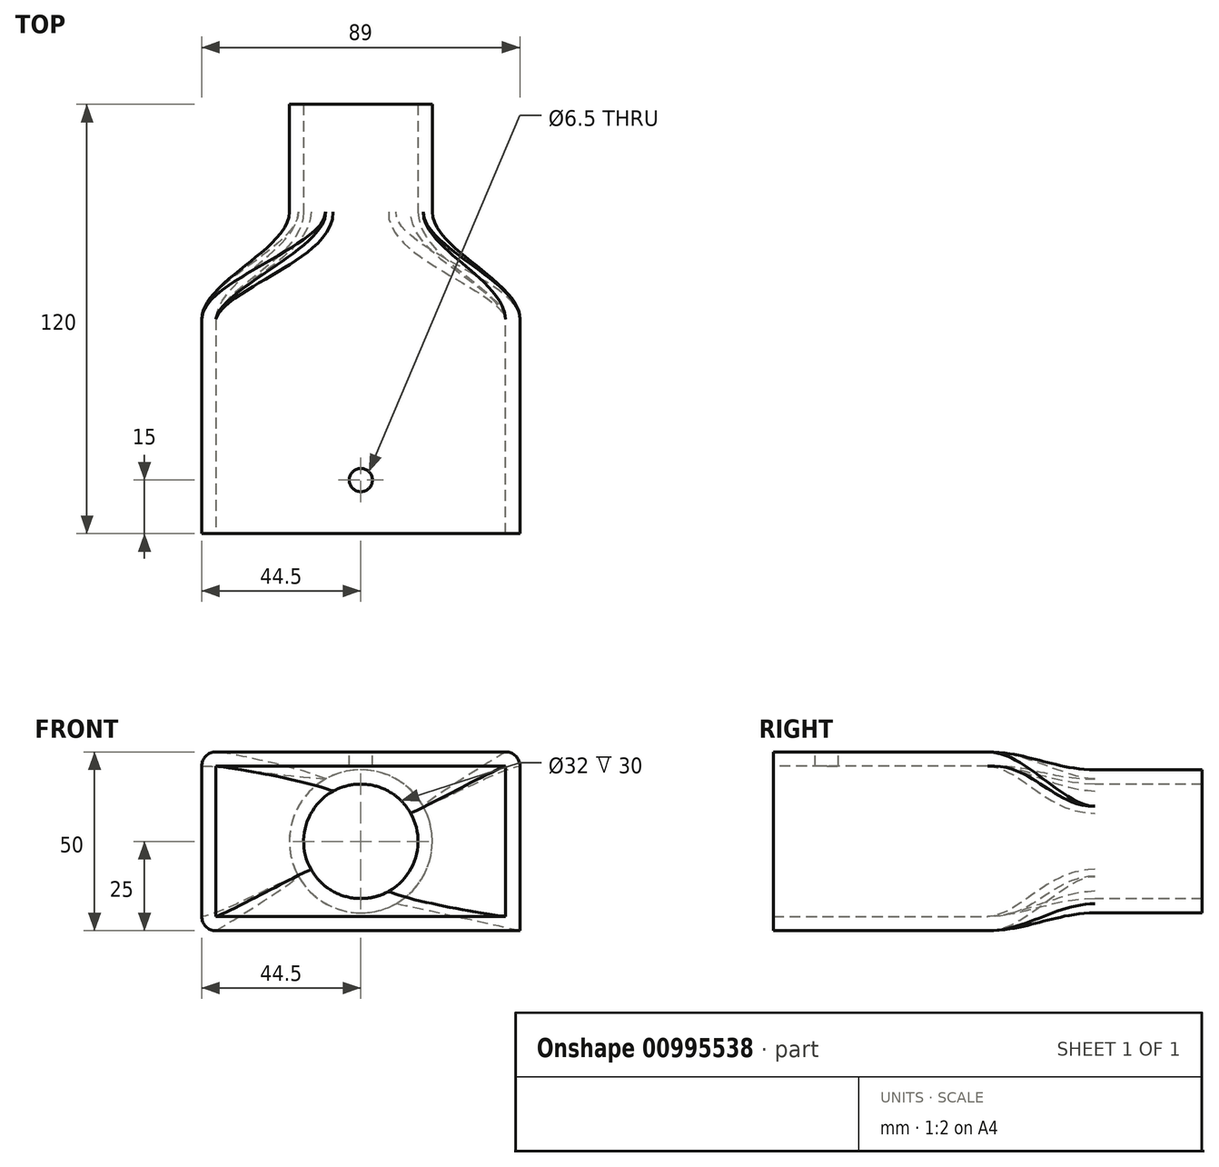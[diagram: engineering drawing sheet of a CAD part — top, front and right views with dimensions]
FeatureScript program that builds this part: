
annotation { "Feature Type Name" : "Feature", "Feature Type Description" : "" }
export const myFeature = defineFeature(function(context is Context, id is Id, definition is map)
    precondition{}
    {
        {
            var Q0;
            Q0=qCreatedBy(makeId("Front.planeOp"),FACE);
            var sketch = newSketch(context, id + "F0", { "sketchPlane" : qUnion([Q0])});
            skLineSegment(sketch, "E0.bottom", {"start": v(40.5, -21) * mm, "end": v(-40.5, -21) * mm, "construction": true});
            skLineSegment(sketch, "E0.top", {"start": v(40.5, 21) * mm, "end": v(-40.5, 21) * mm, "construction": true});
            skLineSegment(sketch, "E0.left", {"start": v(40.5, -21) * mm, "end": v(40.5, 21) * mm, "construction": true});
            skLineSegment(sketch, "E0.right", {"start": v(-40.5, -21) * mm, "end": v(-40.5, 21) * mm, "construction": true});
            skPoint(sketch, "E0.middle", {"position": v(0, 0) * mm});
            skLineSegment(sketch, "E1.0", {"start": v(44.5, 25) * mm, "end": v(-44.5, 25) * mm});
            skLineSegment(sketch, "E1.1", {"start": v(44.5, -25) * mm, "end": v(44.5, 25) * mm});
            skLineSegment(sketch, "E1.2", {"start": v(44.5, -25) * mm, "end": v(-44.5, -25) * mm});
            skLineSegment(sketch, "E1.3", {"start": v(-44.5, -25) * mm, "end": v(-44.5, 25) * mm});
            skSolve(sketch);
        }
        {
            var Q0;
            Q0 = qSketchRegion(id + "F0", true);
            extrude(context, id + "F1", {"entities" : qUnion([Q0]), "depth" : 60 * mm, "offsetDistance" : 25 * mm});
        }
        {
            var Q0;
            Q0=qCreatedBy(makeId("Front.planeOp"),FACE);
            cPlane(context, id + "F2", {"entities" : qUnion([Q0]), "cplaneType" : CPlaneType.OFFSET, "offset" : 30 * mm, "oppositeDirection" : true, "width" : 150 * mm, "height" : 150 * mm});
        }
        {
            var Q0;
            Q0=qCreatedBy(id+"F2.planeOp",FACE);
            var sketch = newSketch(context, id + "F3", { "sketchPlane" : qUnion([Q0])});
            skCircle(sketch, "E2", {"center": v(0, 0) * mm, "radius": 20 * mm});
            skSolve(sketch);
        }
        {
            var Q1;
            Q1=makeQuery(id+"F1.opExtrude","CAP_FACE",FACE,{"disambiguationData":[OSD([sQuery(id+"F0.wireOp",EDGE,"E1.0"),sQuery(id+"F0.wireOp",EDGE,"E1.1"),sQuery(id+"F0.wireOp",EDGE,"E1.2"),sQuery(id+"F0.wireOp",EDGE,"E1.3")])],"isStart":true});
            var Q2;
            Q2 = qSketchRegion(id + "F3", true);
            loft(context, id + "F4", {"operationType" : NewBodyOperationType.ADD, "startCondition" : LoftEndDerivativeType.NORMAL_TO_PROFILE, "startMagnitude" : 1, "endCondition" : LoftEndDerivativeType.NORMAL_TO_PROFILE, "endMagnitude" : 1, "sheetProfilesArray" : [{ "sheetProfileEntities" : qUnion([Q1]) }, { "sheetProfileEntities" : qUnion([Q2]) }]});
        }
        {
            var Q0;
            Q0 = qSketchRegion(id + "F3", true);
            extrude(context, id + "F5", {"entities" : qUnion([Q0]), "operationType" : NewBodyOperationType.ADD, "oppositeDirection" : true, "depth" : 30 * mm, "offsetDistance" : 25 * mm, "hasSecondDirection" : true, "secondDirectionOppositeDirection" : false, "secondDirectionDepth" : 10 * mm});
        }
        {
            var Q0;
            Q0=makeQuery(id+"F4.opLoft","SWEPT_EDGE",EDGE,{"disambiguationData":[OSD([sQuery(id+"F0.wireOp",EDGE,"E1.0"),sQuery(id+"F0.wireOp",EDGE,"E1.2"),sQuery(id+"F0.wireOp",EDGE,"E1.3"),sQuery(id+"F3.wireOp",EDGE,"E2")])]});
            var Q1;
            Q1=makeQuery(id+"F4.opLoft","SWEPT_EDGE",EDGE,{"disambiguationData":[OSD([sQuery(id+"F0.wireOp",EDGE,"E1.1"),sQuery(id+"F0.wireOp",EDGE,"E1.2"),sQuery(id+"F0.wireOp",EDGE,"E1.3"),sQuery(id+"F3.wireOp",EDGE,"E2")])]});
            var Q2;
            Q2=makeQuery(id+"F4.opLoft","SWEPT_EDGE",EDGE,{"disambiguationData":[OSD([sQuery(id+"F0.wireOp",EDGE,"E1.0"),sQuery(id+"F0.wireOp",EDGE,"E1.1"),sQuery(id+"F0.wireOp",EDGE,"E1.2"),sQuery(id+"F3.wireOp",EDGE,"E2")])]});
            var Q3;
            Q3=makeQuery(id+"F4.opLoft","SWEPT_EDGE",EDGE,{"disambiguationData":[OSD([sQuery(id+"F0.wireOp",EDGE,"E1.0"),sQuery(id+"F0.wireOp",EDGE,"E1.1")])]});
            fillet(context, id + "F6", {"entities" : qUnion([Q0, Q1, Q2, Q3]), "radius" : 4 * mm, "tangentPropagation" : true, "allowEdgeOverflow" : false});
        }
        {
            var Q0;
            Q0=makeQuery(id+"F5.opExtrude","CAP_FACE",FACE,{"disambiguationData":[OSD([sQuery(id+"F3.wireOp",EDGE,"E2")])],"isStart":false});
            var Q1;
            Q1=makeQuery(id+"F1.opExtrude","CAP_FACE",FACE,{"disambiguationData":[OSD([sQuery(id+"F0.wireOp",EDGE,"E1.0"),sQuery(id+"F0.wireOp",EDGE,"E1.1"),sQuery(id+"F0.wireOp",EDGE,"E1.2"),sQuery(id+"F0.wireOp",EDGE,"E1.3")])],"isStart":false});
            shell(context, id + "F7", {"entities" : qUnion([Q0, Q1]), "thickness" : 4 * mm});
        }
        {
            var Q0;
            Q0=makeQuery(id+"F1.opExtrude","SWEPT_FACE",FACE,{"disambiguationData":[OSD([sQuery(id+"F0.wireOp",EDGE,"E1.0")])]});
            var sketch = newSketch(context, id + "F8", { "sketchPlane" : qUnion([Q0])});
            skCircle(sketch, "E3", {"center": v(0, -45) * mm, "radius": 3.25 * mm});
            skSolve(sketch);
        }
        {
            var Q0;
            Q0 = qSketchRegion(id + "F8", true);
            extrude(context, id + "F9", {"entities" : qUnion([Q0]), "operationType" : NewBodyOperationType.REMOVE, "endBound" : BoundingType.UP_TO_NEXT, "oppositeDirection" : true, "depth" : 25 * mm, "offsetDistance" : 25 * mm});
        }
    });
